# Revit family: Hager-Univers-IP44-D161-Cl.II-FWB-encl--CH-it
name_source: partatom
category: Equipement électrique
units: mm (PartAtom-declared; Revit-internal decimal feet)

## family parameters
Configuration du panneau = Deux colonnes, circuits au sein
Cote de connecteur circulaire = Utiliser le diamètre
Couper avec des vides une fois chargée = Non
Hôte = Face
Partagée = Non
Point de calcul de pièce = Non
Type d'élément = Tableau de raccordement

## types (1)
- A parete IP44 L800 A1100 P161  - FWB73D1
    Commentaires du type = Univers
    EF000003 - Tipo di montaggio = EV000384 - A parete
    EF000007 - colore = EV000202 - bianco
    EF000008 - Larghezza = 800 mm  [stored 2.62467 ft]
    EF000040 - Altezza = 1100 mm
    EF000049 - profondità = 161 mm  [stored 0.528215 ft]
    EF000116 - numero RAL = 9010
    EF000118 - con piastra di montaggio = Non
    EF000218 - profondità di incasso = 0 mm  [stored 0 ft]
    EF000266 - numero di file = 0
    EF000339 - tipo di copertura = EV004216 - porta
    EF000437 - numero di ingressi per conduttori = 12
    EF001088 - possibilità di applicazione = Oui
    EF001131 - profondità interna = 160 mm
    EF001596 - Attacco Lampada = EV000179 - acciaio
    EF001613 - Integrità del circuito = EV000494 - senza
    EF002950 - Numero moduli DIN = 12
    EF003532 - adatto per uso esterno = Non
    EF004293 - resistenza agli urti = EV006815 - IK09
    EF004427 - numero di moduli = 252
    EF004464 - tipo di porta = EV000494 - senza
    EF005474 - grado di protezione (IP) = EV006418 - IP44
    EF006244 - coperchio/porta trasparente = Non
    EF006306 - con serratura = Non
    EF007800 - adatto per parafulmine = Non
    EF008873 - corrente nominale (In) = 125 A
    EF009170 - spessore materiale scatola = 2 mm  [stored 0.00656168 ft]
    EF009171 - spessore materiale porta/coperchio = 1 mm  [stored 0.00328084 ft]
    EF009212 - esecuzione coperchio = EV009916 - con taglio
    EF009554 - numero delle aperture per la piastra della flangia = 6
    EF015940 - Coprire con rilascio di sovrapressione = Non
    Elévation par défaut = 0 mm  [stored 0 ft]
    Fabricant = Hager
    HG000002 - Con porta = Non
    HG000003 - Gamma = Univers
    HG000004 - Codice produttore = FWB73D1
    HG000006 - Ad incasso = Non
    HG000009 - Porta doppia a battente = Non
    HG000010 - Porte asimmetriche = Non
    HG000023 - Custodia a doppia sezione = Non
    HG000024 - Altezza della sezione inferiore = 800 mm  [stored 2.62467 ft]
    HG000026 - A pavimento = Non
    HG000027 - Altezza dello zoccolo = 0 mm  [stored 0 ft]

note: [stored X ft] marks values corroborated as IEEE doubles in the binary element streams (Revit-internal decimal feet)

## geometry (parser evidence)
native form markers: Sweep x9
no freeform markers — native parametric forms only
